# Revit family: Desks-Teknion-LWCD_Litewood_Carrier_Desk-R2019
name_source: partatom
category: Furniture
units: mm (PartAtom-declared; Revit-internal decimal feet)

## family parameters
Always vertical = Yes
Cut with Voids When Loaded = No
OmniClass Number = 23.40.20.00
OmniClass Title = General Furniture and Specialties
Room Calculation Point = No
Shared = Yes
Work Plane-Based = No

## types (4) — shared parameters
Assembly Code = E2020200
Finish Note = The following finishes can not be changed.
For Additional Finishes please visit = https://assets.teknion.com
Manufacturer = Teknion
Manufacturer Fax = 416.661.4586
Part Number = LWCD
Product Documentation Link = https://assets.teknion.com
Product Line = Litewood
Product Page URL = https://www.teknion.com
Series = Litewood
Sustainability Data = https://www.teknion.com
To render please download texture images found here = https://assets.teknion.com
URL = www.teknion.com
Unit Weight URL = http://www.teknion.com
Warranty = http://www.teknion.com

## per-type parameters (varying)
| type | Description | Metal Leg Finish | Model | No Desktop Riser | PET Liner Finish | Tray Finish | With Desktop Riser |
| No Desktop Riser, Foundry Onyx Metal Leg Finish, 24" Depth, 42" Width | Carrier Desk, No Desktop Riser, Foundry Onyx Metal Leg Finish, Anthracite Finish, Lunar PET Liner Finish, 24" Depth, 42" Width | Paint-Teknion-23-Z-Foundation-Foundry Onyx | LWCDN2442____23__ | Yes | Fabric - Teknion - R6 - Smooth Felt - Lunar | Paint - Teknion - Mica - Anthracite | No |
| No Desktop Riser, Atrium White Metal Leg Finish, 24" Depth, 42" Width | Carrier Desk, No Desktop Riser, Atrium White Metal Leg Finish, Soft Gris Finish, Warm Ash PET Liner Finish, 24" Depth, 42" Width | Paint-Teknion-20-T-Foundation-Atrium White | LWCDN2442____20__ | Yes | Fabric - Teknion - QT - Smooth Felt - River Rock | Paint - Teknion - Foundation - Soft Gris | No |
| With Desktop Riser, Foundry Onyx Metal Leg Finish, 24" Depth, 42" Width | Carrier Desk, With Desktop Riser, Foundry Onyx Metal Leg Finish, Anthracite Finish, Lunar PET Liner Finish, 24" Depth, 42" Width | Paint-Teknion-23-Z-Foundation-Foundry Onyx | LWCDW2442____23__ | No | Fabric - Teknion - R6 - Smooth Felt - Lunar | Paint - Teknion - Mica - Anthracite | Yes |
| With Desktop Riser, Atrium White Metal Leg Finish, 24" Depth, 42" Width | Carrier Desk, With Desktop Riser, Atrium White Metal Leg Finish, Soft Gris Finish, Warm Ash PET Liner Finish, 24" Depth, 42" Width | Paint-Teknion-20-T-Foundation-Atrium White | LWCDW2442____20__ | No | Fabric - Teknion - QT - Smooth Felt - River Rock | Paint - Teknion - Foundation - Soft Gris | Yes |

## geometry (parser evidence)
native form markers: Sweep x3
no freeform markers — native parametric forms only
